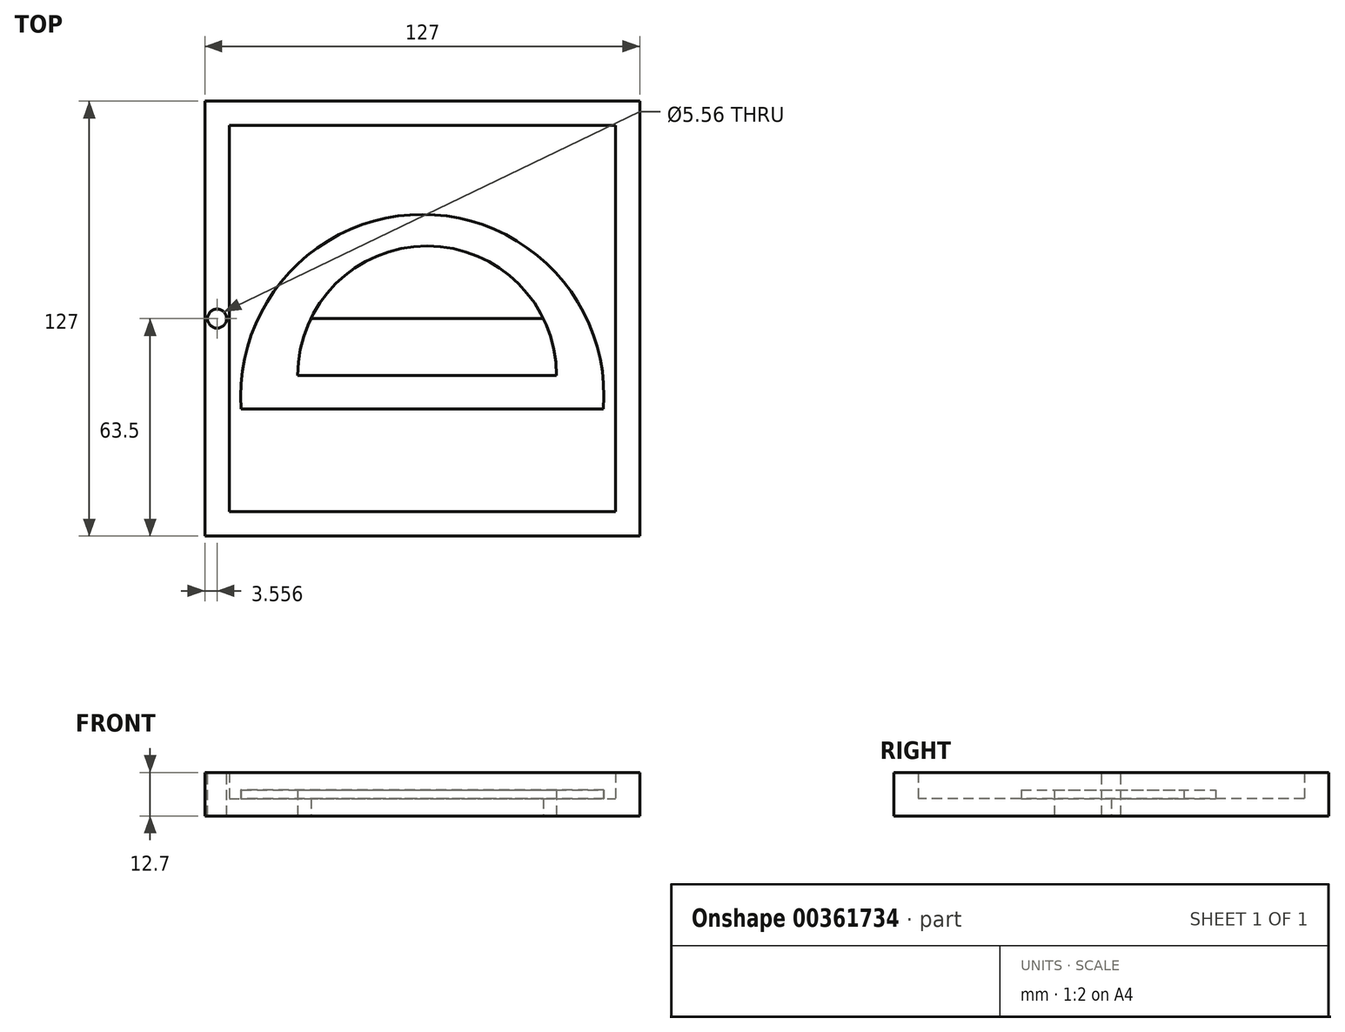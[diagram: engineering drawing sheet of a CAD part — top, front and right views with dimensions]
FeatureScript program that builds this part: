
annotation { "Feature Type Name" : "Feature", "Feature Type Description" : "" }
export const myFeature = defineFeature(function(context is Context, id is Id, definition is map)
    precondition{}
    {
        {
            var Q0;
            Q0=qCreatedBy(makeId("Top.planeOp"),FACE);
            var sketch = newSketch(context, id + "F0", { "sketchPlane" : qUnion([Q0])});
            skLineSegment(sketch, "E0", {"start": v(0, 0) * mm, "end": v(0, -63.5) * mm});
            skLineSegment(sketch, "E1", {"start": v(0, 0) * mm, "end": v(0, 63.5) * mm});
            skLineSegment(sketch, "E2", {"start": v(0, 0) * mm, "end": v(-56.39, 0) * mm});
            skLineSegment(sketch, "E3", {"start": v(-63.5, 0) * mm, "end": v(-63.5, 63.5) * mm});
            skLineSegment(sketch, "E4", {"start": v(-63.5, 63.5) * mm, "end": v(0, 63.5) * mm});
            skLineSegment(sketch, "E5", {"start": v(0, -63.5) * mm, "end": v(-63.5, -63.5) * mm});
            skLineSegment(sketch, "E6", {"start": v(-63.5, -63.5) * mm, "end": v(-63.5, 0) * mm});
            skLineSegment(sketch, "E7", {"start": v(0, 0) * mm, "end": v(63.5, 0) * mm});
            skLineSegment(sketch, "E8", {"start": v(63.5, 0) * mm, "end": v(63.5, -63.5) * mm});
            skLineSegment(sketch, "E9", {"start": v(63.5, -63.5) * mm, "end": v(0, -63.5) * mm});
            skLineSegment(sketch, "E10", {"start": v(63.5, 0) * mm, "end": v(63.5, 63.5) * mm});
            skLineSegment(sketch, "E11", {"start": v(63.5, 63.5) * mm, "end": v(0, 63.5) * mm});
            skLineSegment(sketch, "E12", {"start": v(-56.39, 0) * mm, "end": v(56.39, 0) * mm});
            skPoint(sketch, "E13.start.orphan", {"position": v(-54.36, 0) * mm});
            skPoint(sketch, "E14.start.orphan", {"position": v(54.36, 0) * mm});
            skLineSegment(sketch, "E15", {"start": v(-52.9, -26.35) * mm, "end": v(52.91, -26.35) * mm});
            skArc(sketch, "E16", {"start": v(52.91, -26.35) * mm, "mid": v(0, 30.43) * mm, "end": v(-52.9, -26.35) * mm});
            skLineSegment(sketch, "E17", {"start": v(-36.38, -16.58) * mm, "end": v(39.2, -16.58) * mm});
            skArc(sketch, "E18", {"start": v(39.2, -16.58) * mm, "mid": v(1.4, 21.2) * mm, "end": v(-36.38, -16.58) * mm});
            skLineSegment(sketch, "E19", {"start": v(-56.39, 56.39) * mm, "end": v(-56.39, -56.39) * mm});
            skLineSegment(sketch, "E20", {"start": v(56.39, 56.39) * mm, "end": v(56.39, -56.39) * mm});
            skLineSegment(sketch, "E21", {"start": v(-56.39, -56.39) * mm, "end": v(56.39, -56.39) * mm});
            skLineSegment(sketch, "E22", {"start": v(-56.39, 56.39) * mm, "end": v(56.39, 56.39) * mm});
            skPoint(sketch, "E23.orphan", {"position": v(56.39, 63.5) * mm});
            skPoint(sketch, "E24.orphan", {"position": v(56.39, -63.5) * mm});
            skPoint(sketch, "E25.orphan", {"position": v(-56.39, 63.5) * mm});
            skSolve(sketch);
        }
        {
            var Q0;
            Q0 = qSketchRegion(id + "F0", true);
            extrude(context, id + "F1", {"entities" : qUnion([Q0]), "depth" : 12.7 * mm});
        }
        {
            var Q0;
            {var subQ5=sQuery(id+"F0.wireOp",EDGE,"E16");var subQ6=sQuery(id+"F0.wireOp",EDGE,"E1");var subQ7=makeQuery(id+"F0.imprint","INTERSECT",VERTEX,{"derivedFrom":[subQ6,subQ5]});Q0=makeQuery(id+"F0.imprint","IMPRINT",FACE,{"disambiguationData":[TD([[makeQuery(id+"F0.imprint","IMPRINT",EDGE,{"disambiguationData":[TD([[subQ7,-1.0]])],"derivedFrom":subQ6}),1.0]])]});}
            var Q1;
            {var subQ5=sQuery(id+"F0.wireOp",EDGE,"E16");var subQ6=sQuery(id+"F0.wireOp",EDGE,"E1");var subQ7=makeQuery(id+"F0.imprint","INTERSECT",VERTEX,{"derivedFrom":[subQ6,subQ5]});Q1=makeQuery(id+"F0.imprint","IMPRINT",FACE,{"disambiguationData":[TD([[makeQuery(id+"F0.imprint","IMPRINT",EDGE,{"disambiguationData":[TD([[subQ7,-1.0]])],"derivedFrom":subQ6}),-1.0]])]});}
            var Q2;
            {var subQ1=sQuery(id+"F0.wireOp",EDGE,"E15");var subQ5=sQuery(id+"F0.wireOp",EDGE,"E0");var subQ6=makeQuery(id+"F0.imprint","INTERSECT",VERTEX,{"derivedFrom":[subQ5,subQ1]});Q2=makeQuery(id+"F0.imprint","IMPRINT",FACE,{"disambiguationData":[TD([[makeQuery(id+"F0.imprint","IMPRINT",EDGE,{"disambiguationData":[TD([[subQ6,-1.0]])],"derivedFrom":subQ5}),1.0]])]});}
            var Q3;
            {var subQ1=sQuery(id+"F0.wireOp",EDGE,"E15");var subQ9=sQuery(id+"F0.wireOp",EDGE,"E0");var subQ11=makeQuery(id+"F0.imprint","INTERSECT",VERTEX,{"derivedFrom":[subQ9,subQ1]});Q3=makeQuery(id+"F0.imprint","IMPRINT",FACE,{"disambiguationData":[TD([[makeQuery(id+"F0.imprint","IMPRINT",EDGE,{"disambiguationData":[TD([[subQ11,-1.0]])],"derivedFrom":subQ9}),-1.0]])]});}
            extrude(context, id + "F2", {"entities" : qUnion([Q0, Q1, Q2, Q3]), "operationType" : NewBodyOperationType.ADD, "depth" : 5.08 * mm});
        }
        {
            var Q0;
            {var subQ0=sQuery(id+"F0.wireOp",EDGE,"E18");var subQ1=sQuery(id+"F0.wireOp",EDGE,"E1");var subQ2=makeQuery(id+"F0.imprint","INTERSECT",VERTEX,{"derivedFrom":[subQ1,subQ0]});Q0=makeQuery(id+"F0.imprint","IMPRINT",FACE,{"disambiguationData":[TD([[makeQuery(id+"F0.imprint","IMPRINT",EDGE,{"disambiguationData":[TD([[subQ2,-1.0]])],"derivedFrom":subQ1}),1.0]])]});}
            var Q1;
            {var subQ5=sQuery(id+"F0.wireOp",EDGE,"E0");var subQ7=sQuery(id+"F0.wireOp",EDGE,"E17");var subQ8=makeQuery(id+"F0.imprint","INTERSECT",VERTEX,{"derivedFrom":[subQ5,subQ7]});Q1=makeQuery(id+"F0.imprint","IMPRINT",FACE,{"disambiguationData":[TD([[makeQuery(id+"F0.imprint","IMPRINT",EDGE,{"disambiguationData":[TD([[subQ8,-1.0]])],"derivedFrom":subQ5}),-1.0]])]});}
            var Q2;
            {var subQ5=sQuery(id+"F0.wireOp",EDGE,"E0");var subQ9=sQuery(id+"F0.wireOp",EDGE,"E17");var subQ10=makeQuery(id+"F0.imprint","INTERSECT",VERTEX,{"derivedFrom":[subQ5,subQ9]});Q2=makeQuery(id+"F0.imprint","IMPRINT",FACE,{"disambiguationData":[TD([[makeQuery(id+"F0.imprint","IMPRINT",EDGE,{"disambiguationData":[TD([[subQ10,-1.0]])],"derivedFrom":subQ5}),1.0]])]});}
            var Q3;
            {var subQ0=sQuery(id+"F0.wireOp",EDGE,"E18");var subQ1=sQuery(id+"F0.wireOp",EDGE,"E1");var subQ2=makeQuery(id+"F0.imprint","INTERSECT",VERTEX,{"derivedFrom":[subQ1,subQ0]});Q3=makeQuery(id+"F0.imprint","IMPRINT",FACE,{"disambiguationData":[TD([[makeQuery(id+"F0.imprint","IMPRINT",EDGE,{"disambiguationData":[TD([[subQ2,-1.0]])],"derivedFrom":subQ1}),-1.0]])]});}
            extrude(context, id + "F3", {"entities" : qUnion([Q0, Q1, Q2, Q3]), "operationType" : NewBodyOperationType.ADD, "depth" : 7.62 * mm});
        }
        {
            var Q0;
            {var subQ1=sQuery(id+"F0.wireOp",EDGE,"E1");var subQ3=sQuery(id+"F0.wireOp",EDGE,"E18");var subQ4=makeQuery(id+"F0.imprint","INTERSECT",VERTEX,{"derivedFrom":[subQ1,subQ3]});Q0=makeQuery(id+"F0.imprint","IMPRINT",FACE,{"disambiguationData":[TD([[makeQuery(id+"F0.imprint","IMPRINT",EDGE,{"disambiguationData":[TD([[subQ4,-1.0]])],"derivedFrom":subQ3}),1.0]])]});}
            var Q1;
            {var subQ1=sQuery(id+"F0.wireOp",EDGE,"E1");var subQ3=sQuery(id+"F0.wireOp",EDGE,"E18");var subQ4=makeQuery(id+"F0.imprint","INTERSECT",VERTEX,{"derivedFrom":[subQ1,subQ3]});Q1=makeQuery(id+"F0.imprint","IMPRINT",FACE,{"disambiguationData":[TD([[makeQuery(id+"F0.imprint","IMPRINT",EDGE,{"disambiguationData":[TD([[subQ4,1.0]])],"derivedFrom":subQ3}),1.0]])]});}
            var Q2;
            {var subQ3=sQuery(id+"F0.wireOp",EDGE,"E17");var subQ5=sQuery(id+"F0.wireOp",EDGE,"E18");var subQ7=makeQuery(id+"F0.imprint","INTERSECT",VERTEX,{"disambiguationData":[OD(1.0)],"derivedFrom":[subQ3,subQ5]});Q2=makeQuery(id+"F0.imprint","IMPRINT",FACE,{"disambiguationData":[TD([[makeQuery(id+"F0.imprint","IMPRINT",EDGE,{"disambiguationData":[TD([[subQ7,1.0]])],"derivedFrom":subQ3}),1.0]])]});}
            var Q3;
            {var subQ3=sQuery(id+"F0.wireOp",EDGE,"E17");var subQ5=sQuery(id+"F0.wireOp",EDGE,"E18");var subQ7=makeQuery(id+"F0.imprint","INTERSECT",VERTEX,{"disambiguationData":[OD(0.0)],"derivedFrom":[subQ3,subQ5]});Q3=makeQuery(id+"F0.imprint","IMPRINT",FACE,{"disambiguationData":[TD([[makeQuery(id+"F0.imprint","IMPRINT",EDGE,{"disambiguationData":[TD([[subQ7,-1.0]])],"derivedFrom":subQ3}),1.0]])]});}
            extrude(context, id + "F4", {"entities" : qUnion([Q0, Q1, Q2, Q3]), "operationType" : NewBodyOperationType.ADD, "depth" : 5.08 * mm});
        }
        {
            var Q0;
            Q0=makeQuery(id+"F1.opExtrude","CAP_FACE",FACE,{"disambiguationData":[OSD([sQuery(id+"F0.wireOp",EDGE,"E3"),sQuery(id+"F0.wireOp",EDGE,"E4"),sQuery(id+"F0.wireOp",EDGE,"E5"),sQuery(id+"F0.wireOp",EDGE,"E6"),sQuery(id+"F0.wireOp",EDGE,"E8"),sQuery(id+"F0.wireOp",EDGE,"E9"),sQuery(id+"F0.wireOp",EDGE,"E10"),sQuery(id+"F0.wireOp",EDGE,"E11"),sQuery(id+"F0.wireOp",EDGE,"E19"),sQuery(id+"F0.wireOp",EDGE,"E20"),sQuery(id+"F0.wireOp",EDGE,"E21"),sQuery(id+"F0.wireOp",EDGE,"E22")])],"isStart":false});
            var sketch = newSketch(context, id + "F5", { "sketchPlane" : qUnion([Q0])});
            skLineSegment(sketch, "E26.0", {"start": v(-56.39, 0) * mm, "end": v(56.39, 0) * mm});
            skLineSegment(sketch, "E27", {"start": v(-56.39, 0) * mm, "end": v(-63.5, 0) * mm});
            skCircle(sketch, "E28", {"center": v(-59.94, 0) * mm, "radius": 2.78 * mm});
            skSolve(sketch);
        }
        {
            var Q0;
            Q0 = qSketchRegion(id + "F5", true);
            extrude(context, id + "F6", {"entities" : qUnion([Q0]), "operationType" : NewBodyOperationType.REMOVE, "oppositeDirection" : true, "depth" : 25.4 * mm});
        }
    });
